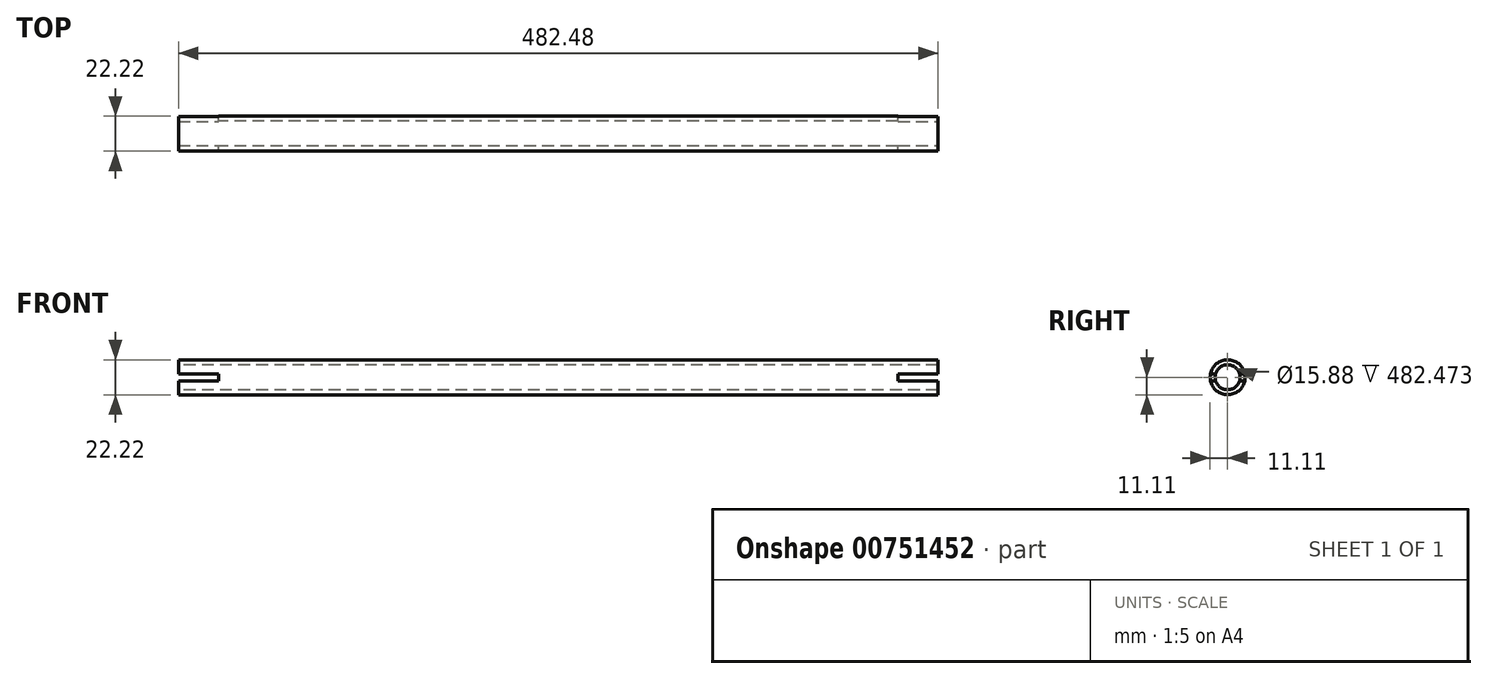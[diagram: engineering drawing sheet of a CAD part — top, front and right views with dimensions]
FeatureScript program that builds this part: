
annotation { "Feature Type Name" : "Feature", "Feature Type Description" : "" }
export const myFeature = defineFeature(function(context is Context, id is Id, definition is map)
    precondition{}
    {
        {
            var Q0;
            Q0=qCreatedBy(makeId("Right.planeOp"),FACE);
            var sketch = newSketch(context, id + "F0", { "sketchPlane" : qUnion([Q0])});
            skCircle(sketch, "E0", {"center": v(0, 0) * mm, "radius": 7.94 * mm});
            skCircle(sketch, "E1", {"center": v(0, 0) * mm, "radius": 11.11 * mm});
            skSolve(sketch);
        }
        {
            var Q0;
            Q0=makeQuery(id+"F0.imprint","IMPRINT",FACE,{"disambiguationData":[TD([[makeQuery(id+"F0.imprint","IMPRINT",EDGE,{"derivedFrom":sQuery(id+"F0.wireOp",EDGE,"E0")}),-1.0]])]});
            extrude(context, id + "F1", {"entities" : qUnion([Q0]), "depth" : 241.24 * mm, "offsetDistance" : 25.4 * mm, "hasSecondDirection" : true, "secondDirectionOppositeDirection" : true, "secondDirectionDepth" : 241.24 * mm});
        }
        {
            var Q0;
            Q0=makeQuery(id+"F1.opExtrude","CAP_FACE",FACE,{"disambiguationData":[OSD([sQuery(id+"F0.wireOp",EDGE,"E0"),sQuery(id+"F0.wireOp",EDGE,"E1")])],"isStart":false});
            var sketch = newSketch(context, id + "F2", { "sketchPlane" : qUnion([Q0])});
            skLineSegment(sketch, "E2.bottom", {"start": v(-11.11, 2.22) * mm, "end": v(11.11, 2.22) * mm});
            skLineSegment(sketch, "E2.top", {"start": v(-11.11, -2.22) * mm, "end": v(11.11, -2.22) * mm});
            skLineSegment(sketch, "E2.left", {"start": v(-11.11, 2.22) * mm, "end": v(-11.11, -2.22) * mm});
            skLineSegment(sketch, "E2.right", {"start": v(11.11, 2.22) * mm, "end": v(11.11, -2.22) * mm});
            skPoint(sketch, "E3", {"position": v(-11.11, 0) * mm});
            skPoint(sketch, "E4", {"position": v(11.11, 0) * mm});
            skSolve(sketch);
        }
        {
            var Q0;
            {var subQ0=sQuery(id+"F2.wireOp",EDGE,"E2.bottom");var subQ1=makeQuery(id+"F1.opExtrude","CAP_EDGE",EDGE,{"disambiguationData":[OSD([sQuery(id+"F0.wireOp",EDGE,"E1")])],"isStart":false});var subQ2=makeQuery(id+"F2.imprint","INTERSECT",VERTEX,{"disambiguationData":[OD(0.0)],"derivedFrom":[subQ1,subQ0]});Q0=makeQuery(id+"F2.imprint","IMPRINT",FACE,{"disambiguationData":[TD([[makeQuery(id+"F2.imprint","IMPRINT",EDGE,{"disambiguationData":[TD([[subQ2,-1.0]])],"derivedFrom":subQ0}),-1.0]])]});}
            var Q1;
            {var subQ0=sQuery(id+"F2.wireOp",EDGE,"E2.bottom");var subQ1=makeQuery(id+"F1.opExtrude","CAP_EDGE",EDGE,{"disambiguationData":[OSD([sQuery(id+"F0.wireOp",EDGE,"E1")])],"isStart":false});var subQ2=makeQuery(id+"F2.imprint","INTERSECT",VERTEX,{"disambiguationData":[OD(1.0)],"derivedFrom":[subQ1,subQ0]});Q1=makeQuery(id+"F2.imprint","IMPRINT",FACE,{"disambiguationData":[TD([[makeQuery(id+"F2.imprint","IMPRINT",EDGE,{"disambiguationData":[TD([[subQ2,1.0]])],"derivedFrom":subQ0}),-1.0]])]});}
            extrude(context, id + "F3", {"entities" : qUnion([Q0, Q1]), "operationType" : NewBodyOperationType.REMOVE, "endBound" : BoundingType.THROUGH_ALL, "oppositeDirection" : true, "depth" : 25.4 * mm, "offsetDistance" : 25.4 * mm});
        }
        {
            var Q0;
            {var subQ0=sQuery(id+"F2.wireOp",EDGE,"E2.bottom");var subQ1=makeQuery(id+"F1.opExtrude","CAP_EDGE",EDGE,{"disambiguationData":[OSD([sQuery(id+"F0.wireOp",EDGE,"E1")])],"isStart":false});var subQ2=makeQuery(id+"F2.imprint","INTERSECT",VERTEX,{"disambiguationData":[OD(1.0)],"derivedFrom":[subQ1,subQ0]});Q0=makeQuery(id+"F2.imprint","IMPRINT",FACE,{"disambiguationData":[TD([[makeQuery(id+"F2.imprint","IMPRINT",EDGE,{"disambiguationData":[TD([[subQ2,1.0]])],"derivedFrom":subQ0}),-1.0]])]});}
            var Q1;
            {var subQ0=sQuery(id+"F2.wireOp",EDGE,"E2.bottom");var subQ1=makeQuery(id+"F1.opExtrude","CAP_EDGE",EDGE,{"disambiguationData":[OSD([sQuery(id+"F0.wireOp",EDGE,"E1")])],"isStart":false});var subQ2=makeQuery(id+"F2.imprint","INTERSECT",VERTEX,{"disambiguationData":[OD(0.0)],"derivedFrom":[subQ1,subQ0]});Q1=makeQuery(id+"F2.imprint","IMPRINT",FACE,{"disambiguationData":[TD([[makeQuery(id+"F2.imprint","IMPRINT",EDGE,{"disambiguationData":[TD([[subQ2,-1.0]])],"derivedFrom":subQ0}),-1.0]])]});}
            extrude(context, id + "F4", {"entities" : qUnion([Q0, Q1]), "operationType" : NewBodyOperationType.ADD, "oppositeDirection" : true, "depth" : 457.07 * mm, "offsetDistance" : 25.4 * mm});
        }
        {
            var Q0;
            {var subQ0=sQuery(id+"F2.wireOp",EDGE,"E2.bottom");var subQ1=makeQuery(id+"F1.opExtrude","CAP_EDGE",EDGE,{"disambiguationData":[OSD([sQuery(id+"F0.wireOp",EDGE,"E1")])],"isStart":false});var subQ2=makeQuery(id+"F2.imprint","INTERSECT",VERTEX,{"disambiguationData":[OD(0.0)],"derivedFrom":[subQ1,subQ0]});Q0=makeQuery(id+"F2.imprint","IMPRINT",FACE,{"disambiguationData":[TD([[makeQuery(id+"F2.imprint","IMPRINT",EDGE,{"disambiguationData":[TD([[subQ2,-1.0]])],"derivedFrom":subQ0}),-1.0]])]});}
            var Q1;
            {var subQ0=sQuery(id+"F2.wireOp",EDGE,"E2.bottom");var subQ1=makeQuery(id+"F1.opExtrude","CAP_EDGE",EDGE,{"disambiguationData":[OSD([sQuery(id+"F0.wireOp",EDGE,"E1")])],"isStart":false});var subQ2=makeQuery(id+"F2.imprint","INTERSECT",VERTEX,{"disambiguationData":[OD(1.0)],"derivedFrom":[subQ1,subQ0]});Q1=makeQuery(id+"F2.imprint","IMPRINT",FACE,{"disambiguationData":[TD([[makeQuery(id+"F2.imprint","IMPRINT",EDGE,{"disambiguationData":[TD([[subQ2,1.0]])],"derivedFrom":subQ0}),-1.0]])]});}
            extrude(context, id + "F5", {"entities" : qUnion([Q0, Q1]), "operationType" : NewBodyOperationType.REMOVE, "oppositeDirection" : true, "depth" : 25.4 * mm, "offsetDistance" : 25.4 * mm});
        }
    });
